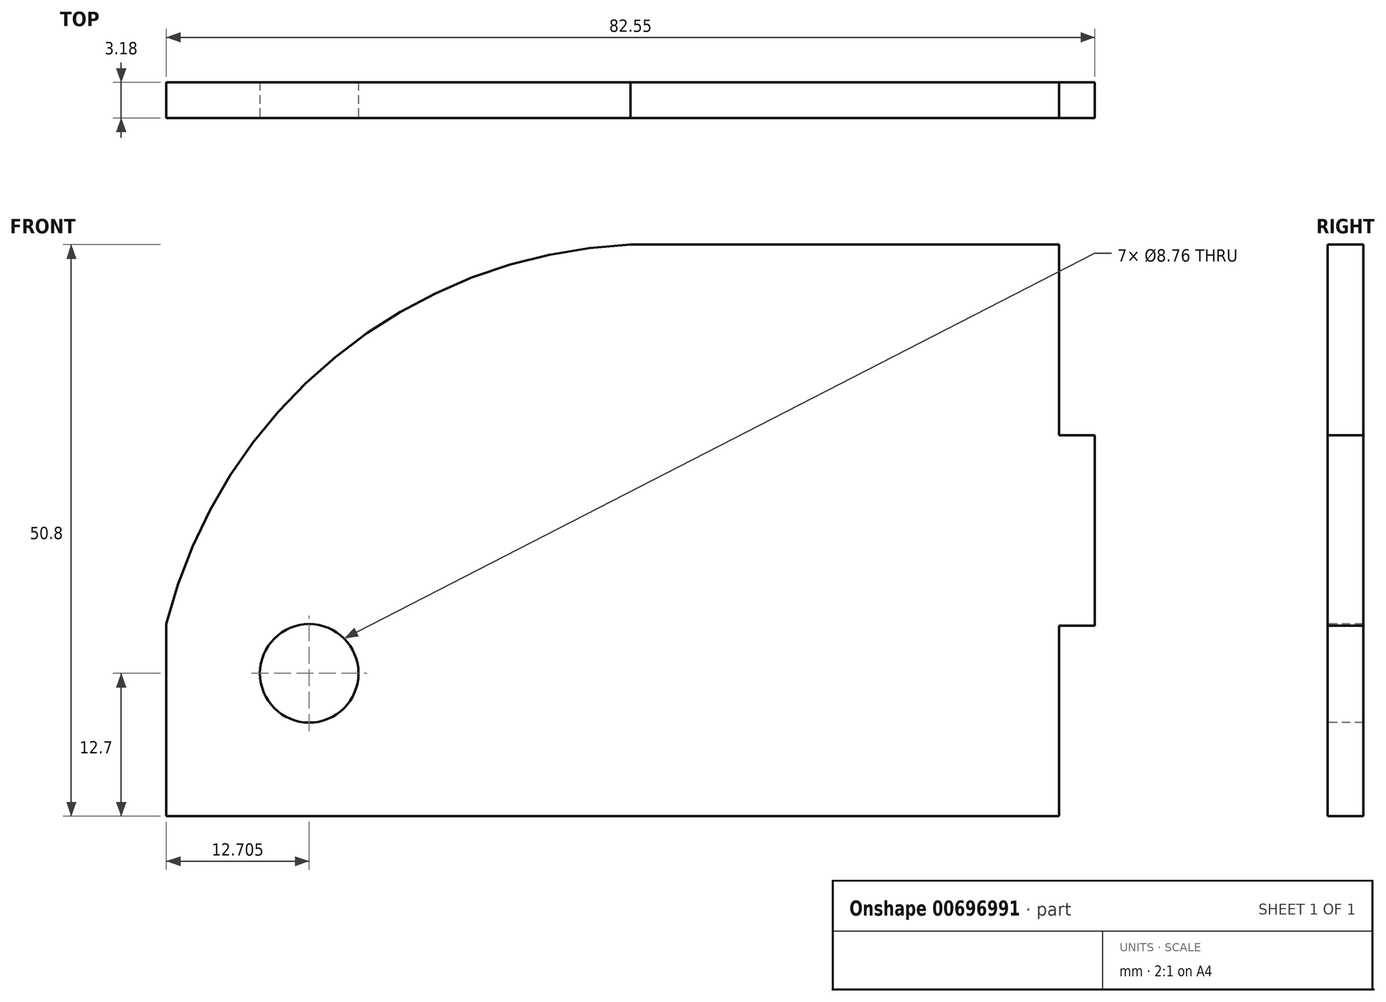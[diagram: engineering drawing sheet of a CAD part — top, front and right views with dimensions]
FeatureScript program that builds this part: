
annotation { "Feature Type Name" : "Feature", "Feature Type Description" : "" }
export const myFeature = defineFeature(function(context is Context, id is Id, definition is map)
    precondition{}
    {
        {
            var Q0;
            Q0=qCreatedBy(makeId("Front.planeOp"),FACE);
            var sketch = newSketch(context, id + "F0", { "sketchPlane" : qUnion([Q0])});
            skLineSegment(sketch, "E0.bottom", {"start": v(41.27, 25.4) * mm, "end": v(-41.28, 25.4) * mm});
            skLineSegment(sketch, "E0.top", {"start": v(41.28, -25.4) * mm, "end": v(-41.27, -25.4) * mm});
            skLineSegment(sketch, "E0.left", {"start": v(41.27, 25.4) * mm, "end": v(41.28, -25.4) * mm});
            skLineSegment(sketch, "E0.right", {"start": v(-41.28, 25.4) * mm, "end": v(-41.27, -25.4) * mm});
            skPoint(sketch, "E0.middle", {"position": v(0, 0) * mm});
            skSolve(sketch);
        }
        {
            var Q0;
            Q0 = qSketchRegion(id + "F0", true);
            extrude(context, id + "F1", {"entities" : qUnion([Q0]), "depth" : 3.17 * mm, "offsetDistance" : 25.4 * mm});
        }
        {
            var Q0;
            Q0=makeQuery(id+"F1.opExtrude","CAP_FACE",FACE,{"disambiguationData":[OSD([sQuery(id+"F0.wireOp",EDGE,"E0.bottom"),sQuery(id+"F0.wireOp",EDGE,"E0.top"),sQuery(id+"F0.wireOp",EDGE,"E0.left"),sQuery(id+"F0.wireOp",EDGE,"E0.right")])],"isStart":false});
            var sketch = newSketch(context, id + "F2", { "sketchPlane" : qUnion([Q0])});
            skCircle(sketch, "E1", {"center": v(-28.57, -12.7) * mm, "radius": 4.38 * mm});
            skSolve(sketch);
        }
        {
            var Q0;
            Q0=makeQuery(id+"F2.imprint","IMPRINT",FACE,{"disambiguationData":[TD([[makeQuery(id+"F2.imprint","IMPRINT",EDGE,{"derivedFrom":sQuery(id+"F2.wireOp",EDGE,"E1")}),1.0]])]});
            extrude(context, id + "F3", {"entities" : qUnion([Q0]), "operationType" : NewBodyOperationType.REMOVE, "oppositeDirection" : true, "depth" : 3.17 * mm, "offsetDistance" : 25.4 * mm});
        }
        {
            var Q0;
            Q0=makeQuery(id+"F1.opExtrude","CAP_FACE",FACE,{"disambiguationData":[OSD([sQuery(id+"F0.wireOp",EDGE,"E0.bottom"),sQuery(id+"F0.wireOp",EDGE,"E0.top"),sQuery(id+"F0.wireOp",EDGE,"E0.left"),sQuery(id+"F0.wireOp",EDGE,"E0.right")])],"isStart":false});
            var sketch = newSketch(context, id + "F4", { "sketchPlane" : qUnion([Q0])});
            skLineSegment(sketch, "E2", {"start": v(-28.67, -8.32) * mm, "end": v(-41.27, -8.32) * mm, "construction": true});
            skArc(sketch, "E3", {"start": v(0, 25.4) * mm, "mid": v(-26.25, 15.41) * mm, "end": v(-41.27, -8.32) * mm});
            skLineSegment(sketch, "E4", {"start": v(-41.28, -8.32) * mm, "end": v(-41.28, 25.4) * mm});
            skLineSegment(sketch, "E5", {"start": v(-41.28, 25.4) * mm, "end": v(0, 25.4) * mm});
            skSolve(sketch);
        }
        {
            var Q0;
            Q0=makeQuery(id+"F4.imprint","IMPRINT",FACE,{"disambiguationData":[TD([[makeQuery(id+"F4.imprint","IMPRINT",EDGE,{"derivedFrom":sQuery(id+"F4.wireOp",EDGE,"E3")}),-1.0]])]});
            extrude(context, id + "F5", {"entities" : qUnion([Q0]), "operationType" : NewBodyOperationType.REMOVE, "oppositeDirection" : true, "depth" : 3.17 * mm, "offsetDistance" : 25.4 * mm});
        }
        {
            var Q0;
            Q0=makeQuery(id+"F1.opExtrude","CAP_FACE",FACE,{"disambiguationData":[OSD([sQuery(id+"F0.wireOp",EDGE,"E0.bottom"),sQuery(id+"F0.wireOp",EDGE,"E0.top"),sQuery(id+"F0.wireOp",EDGE,"E0.left"),sQuery(id+"F0.wireOp",EDGE,"E0.right")])],"isStart":false});
            var sketch = newSketch(context, id + "F6", { "sketchPlane" : qUnion([Q0])});
            skLineSegment(sketch, "E6", {"start": v(41.27, 25.4) * mm, "end": v(41.28, -25.4) * mm, "construction": true});
            skLineSegment(sketch, "E7", {"start": v(41.27, 25.4) * mm, "end": v(38.1, 25.4) * mm});
            skLineSegment(sketch, "E8", {"start": v(38.1, 25.4) * mm, "end": v(38.1, 8.47) * mm, "construction": true});
            skLineSegment(sketch, "E9", {"start": v(38.1, 8.47) * mm, "end": v(38.1, -8.47) * mm, "construction": true});
            skLineSegment(sketch, "E10", {"start": v(38.1, -8.47) * mm, "end": v(38.1, -25.4) * mm, "construction": true});
            skLineSegment(sketch, "E11.bottom", {"start": v(38.1, 8.47) * mm, "end": v(41.27, 8.47) * mm});
            skLineSegment(sketch, "E11.top", {"start": v(38.1, 25.4) * mm, "end": v(41.27, 25.4) * mm});
            skLineSegment(sketch, "E11.left", {"start": v(38.1, 8.47) * mm, "end": v(38.1, 25.4) * mm});
            skLineSegment(sketch, "E11.right", {"start": v(41.27, 8.47) * mm, "end": v(41.27, 25.4) * mm});
            skLineSegment(sketch, "E12.bottom", {"start": v(38.1, -8.47) * mm, "end": v(41.28, -8.47) * mm});
            skLineSegment(sketch, "E12.top", {"start": v(38.1, -25.4) * mm, "end": v(41.28, -25.4) * mm});
            skLineSegment(sketch, "E12.left", {"start": v(38.1, -8.47) * mm, "end": v(38.1, -25.4) * mm});
            skLineSegment(sketch, "E12.right", {"start": v(41.28, -8.47) * mm, "end": v(41.28, -25.4) * mm});
            skSolve(sketch);
        }
        {
            var Q0;
            Q0=makeQuery(id+"F6.imprint","IMPRINT",FACE,{"disambiguationData":[TD([[makeQuery(id+"F6.imprint","IMPRINT",EDGE,{"derivedFrom":sQuery(id+"F6.wireOp",EDGE,"E11.bottom")}),1.0]])]});
            var Q1;
            Q1=makeQuery(id+"F6.imprint","IMPRINT",FACE,{"disambiguationData":[TD([[makeQuery(id+"F6.imprint","IMPRINT",EDGE,{"derivedFrom":sQuery(id+"F6.wireOp",EDGE,"E12.bottom")}),-1.0]])]});
            extrude(context, id + "F7", {"entities" : qUnion([Q0, Q1]), "operationType" : NewBodyOperationType.REMOVE, "oppositeDirection" : true, "depth" : 3.17 * mm, "offsetDistance" : 25.4 * mm});
        }
    });
